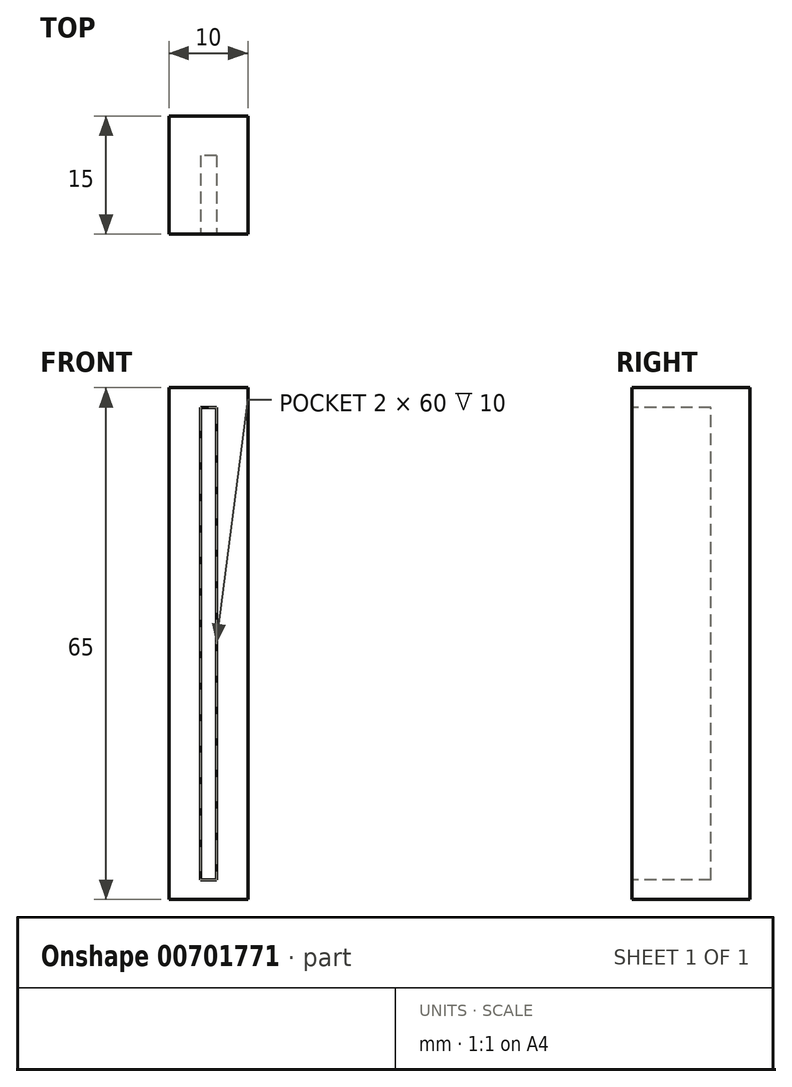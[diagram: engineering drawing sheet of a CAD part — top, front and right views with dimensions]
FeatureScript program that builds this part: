
annotation { "Feature Type Name" : "Feature", "Feature Type Description" : "" }
export const myFeature = defineFeature(function(context is Context, id is Id, definition is map)
    precondition{}
    {
        {
            var Q0;
            Q0=qCreatedBy(makeId("Front.planeOp"),FACE);
            var sketch = newSketch(context, id + "F0", { "sketchPlane" : qUnion([Q0])});
            skLineSegment(sketch, "E0.bottom", {"start": v(-5, 32.5) * mm, "end": v(5, 32.5) * mm});
            skLineSegment(sketch, "E0.top", {"start": v(-5, -32.5) * mm, "end": v(5, -32.5) * mm});
            skLineSegment(sketch, "E0.left", {"start": v(-5, 32.5) * mm, "end": v(-5, -32.5) * mm});
            skLineSegment(sketch, "E0.right", {"start": v(5, 32.5) * mm, "end": v(5, -32.5) * mm});
            skPoint(sketch, "E0.middle", {"position": v(0, 0) * mm});
            skSolve(sketch);
        }
        {
            var Q0;
            Q0=makeQuery(id+"F0.imprint","IMPRINT",FACE,{"disambiguationData":[TD([[makeQuery(id+"F0.imprint","IMPRINT",EDGE,{"derivedFrom":sQuery(id+"F0.wireOp",EDGE,"E0.bottom")}),-1.0]])]});
            var Q1;
            Q1=makeQuery(id+"F0.imprint","IMPRINT",FACE,{"disambiguationData":[TD([[makeQuery(id+"F0.imprint","IMPRINT",EDGE,{"derivedFrom":sQuery(id+"F0.wireOp",EDGE,"p4wl24iP-lMOd-Ku6s-9Q9M-5x0dqJ1ETdzH.bottom")}),-1.0]])]});
            extrude(context, id + "F1", {"entities" : qUnion([Q0, Q1]), "depth" : 15 * mm});
        }
        {
            var Q0;
            Q0=makeQuery(id+"F1.opExtrude","CAP_FACE",FACE,{"disambiguationData":[OSD([sQuery(id+"F0.wireOp",EDGE,"E0.bottom"),sQuery(id+"F0.wireOp",EDGE,"E0.top"),sQuery(id+"F0.wireOp",EDGE,"E0.left"),sQuery(id+"F0.wireOp",EDGE,"E0.right")])],"isStart":false});
            var sketch = newSketch(context, id + "F2", { "sketchPlane" : qUnion([Q0])});
            skLineSegment(sketch, "E1.bottom", {"start": v(1, -30) * mm, "end": v(-1, -30) * mm});
            skLineSegment(sketch, "E1.top", {"start": v(1, 30) * mm, "end": v(-1, 30) * mm});
            skLineSegment(sketch, "E1.left", {"start": v(1, -30) * mm, "end": v(1, 30) * mm});
            skLineSegment(sketch, "E1.right", {"start": v(-1, -30) * mm, "end": v(-1, 30) * mm});
            skPoint(sketch, "E2", {"position": v(0, 0) * mm});
            skSolve(sketch);
        }
        {
            var Q0;
            Q0=makeQuery(id+"F2.imprint","IMPRINT",FACE,{"disambiguationData":[TD([[makeQuery(id+"F2.imprint","IMPRINT",EDGE,{"derivedFrom":sQuery(id+"F2.wireOp",EDGE,"E1.bottom")}),-1.0]])]});
            extrude(context, id + "F3", {"entities" : qUnion([Q0]), "operationType" : NewBodyOperationType.REMOVE, "oppositeDirection" : true, "depth" : 10 * mm});
        }
        {
            var Q0;
            Q0=makeQuery(id+"F3.boolean.opBoolean","COPY",FACE,{"derivedFrom":makeQuery(id+"F3.opExtrude","CAP_FACE",FACE,{"disambiguationData":[OSD([sQuery(id+"F2.wireOp",EDGE,"E1.bottom"),sQuery(id+"F2.wireOp",EDGE,"E1.top"),sQuery(id+"F2.wireOp",EDGE,"E1.left"),sQuery(id+"F2.wireOp",EDGE,"E1.right")])],"isStart":false})});
            var sketch = newSketch(context, id + "F4", { "sketchPlane" : qUnion([Q0])});
            skPoint(sketch, "E3", {"position": v(0, 0) * mm});
            skSolve(sketch);
        }
    });
